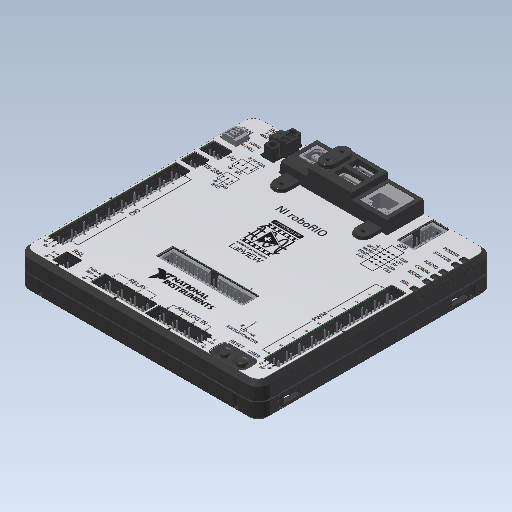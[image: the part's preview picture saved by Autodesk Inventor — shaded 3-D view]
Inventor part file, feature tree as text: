
AUTODESK INVENTOR PART (.ipt)
format: ipt  version: 2020 (Build 240168000, 168)  size: 41,393,664 bytes
history: native  units: in
note: dims shown in document units (in); Inventor stores cm internally (conversion verified against a paired STEP export)
features: imported_body x15, other x4, sketch x1
ambient origin geometry x8: Origin, YZ Plane, XZ Plane, XY Plane, X Axis, Y Axis, Z Axis, Center Point
bodies: Solid1 (feature_tree), Solid2 (feature_tree), Solid3 (feature_tree), Solid4 (feature_tree), Solid5 (feature_tree), Solid6 (feature_tree), Solid7 (feature_tree), Solid8 (feature_tree), Solid9 (feature_tree), Solid10 (feature_tree), Solid11 (feature_tree), Solid12 (feature_tree), Solid13 (feature_tree), Solid14 (feature_tree), Solid15 (feature_tree), Solid16 (feature_tree)
feature tree (20):
  other  "cd_roborio1"
  other  "Decal1"
  imported_body  "Base1"
  imported_body  "Base2"
  imported_body  "Base3"
  imported_body  "Base4"
  imported_body  "Base5"
  other  "roboRIO CASE"
  imported_body  "Base7"
  imported_body  "Base8"
  imported_body  "Base9"
  imported_body  "Base10"
  imported_body  "Base11"
  imported_body  "Base12"
  imported_body  "Base13"
  imported_body  "Base14"
  imported_body  "Base15"
  imported_body  "Base16"
  sketch  "Sketch1"
  other  "Image1"
